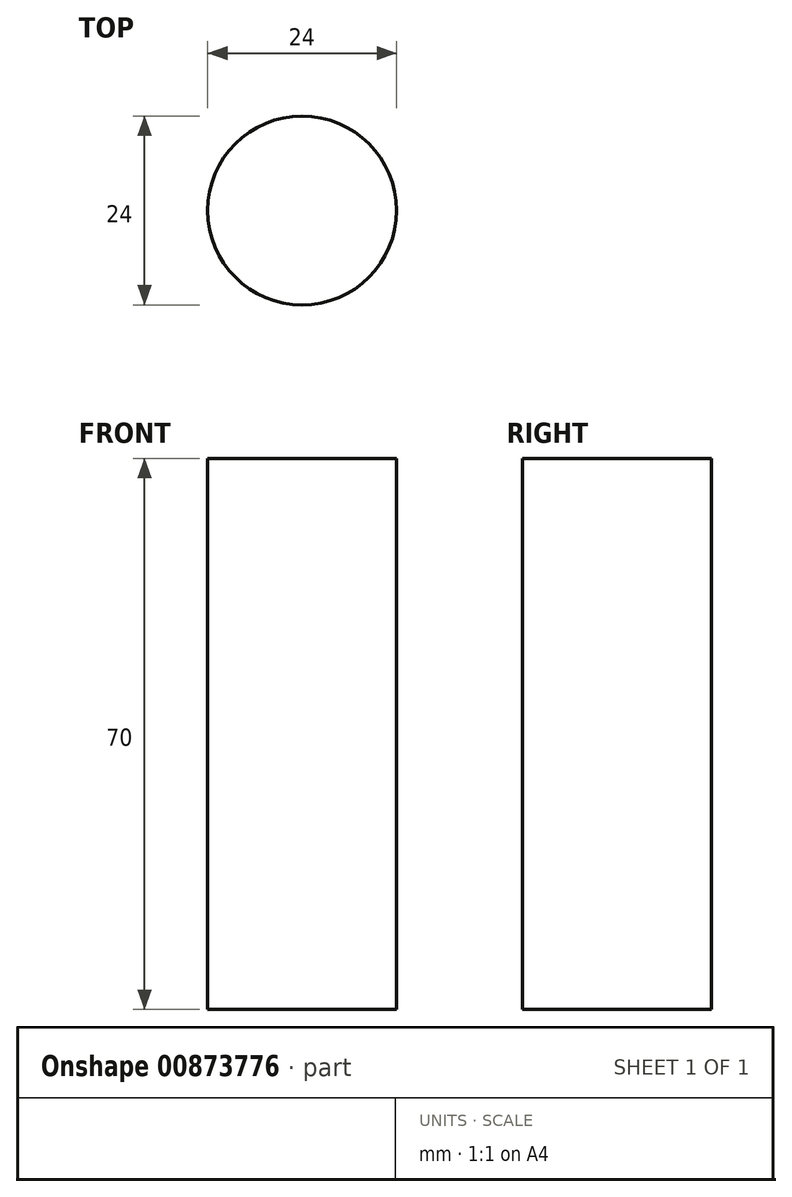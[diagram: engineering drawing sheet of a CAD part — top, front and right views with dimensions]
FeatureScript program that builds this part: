
annotation { "Feature Type Name" : "Feature", "Feature Type Description" : "" }
export const myFeature = defineFeature(function(context is Context, id is Id, definition is map)
    precondition{}
    {
        {
            var Q0;
            Q0=qCreatedBy(makeId("Top.planeOp"),FACE);
            var sketch = newSketch(context, id + "F0", { "sketchPlane" : qUnion([Q0])});
            skCircle(sketch, "E0", {"center": v(0, 0) * mm, "radius": 12 * mm});
            skSolve(sketch);
        }
        {
            var Q0;
            Q0 = qSketchRegion(id + "F0", true);
            extrude(context, id + "F1", {"entities" : qUnion([Q0]), "depth" : 70 * mm, "offsetDistance" : 25 * mm});
        }
    });
